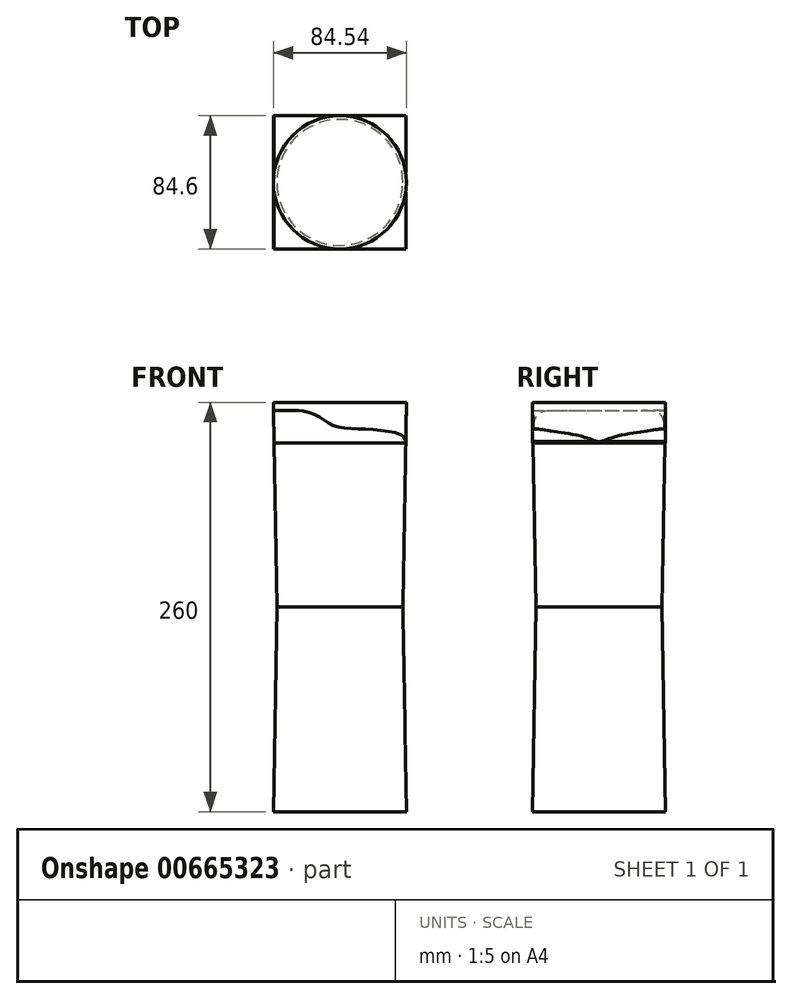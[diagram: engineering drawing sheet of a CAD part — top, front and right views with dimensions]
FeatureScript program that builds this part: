
annotation { "Feature Type Name" : "Feature", "Feature Type Description" : "" }
export const myFeature = defineFeature(function(context is Context, id is Id, definition is map)
    precondition{}
    {
        {
            var Q0;
            Q0=qCreatedBy(makeId("Top.planeOp"),FACE);
            var sketch = newSketch(context, id + "F0", { "sketchPlane" : qUnion([Q0])});
            skCircle(sketch, "E0", {"center": v(0, 0) * mm, "radius": 40 * mm});
            skSolve(sketch);
        }
        {
            var Q0;
            Q0=makeQuery(id+"F0.imprint","IMPRINT",FACE,{"disambiguationData":[TD([[makeQuery(id+"F0.imprint","IMPRINT",EDGE,{"derivedFrom":sQuery(id+"F0.wireOp",EDGE,"E0")}),1.0]])]});
            extrude(context, id + "F1", {"entities" : qUnion([Q0]), "endBound" : BoundingType.SYMMETRIC, "depth" : 260 * mm, "offsetDistance" : 25 * mm, "hasDraft" : true, "draftAngle" : 1 * degree});
        }
        {
            var Q0;
            Q0=qCreatedBy(makeId("Front.planeOp"),FACE);
            var sketch = newSketch(context, id + "F2", { "sketchPlane" : qUnion([Q0])});
            skLineSegment(sketch, "E1", {"start": v(-41.82, 104.3) * mm, "end": v(41.83, 104.3) * mm});
            skLineSegment(sketch, "E2", {"start": v(41.83, 104.3) * mm, "end": v(41.83, 105.18) * mm});
            skFitSpline(sketch, "E3", {"points": [v(41.83, 105.18) * mm, v(39.98, 108.81) * mm, v(17.77, 112.92) * mm, v(-4.2, 115.37) * mm, v(-17.46, 123.04) * mm, v(-41.82, 124.75) * mm], "startDerivative": vector(-6.46, 38.94) * mm, "endDerivative": vector(-110.85, -2.96) * mm});
            skLineSegment(sketch, "E4", {"start": v(-41.82, 124.75) * mm, "end": v(-42.18, 124.73) * mm});
            skLineSegment(sketch, "E5", {"start": v(-42.18, 124.73) * mm, "end": v(-41.82, 104.3) * mm});
            skSolve(sketch);
        }
        {
            var Q0;
            Q0 = qSketchRegion(id + "F2", true);
            extrude(context, id + "F3", {"entities" : qUnion([Q0]), "operationType" : NewBodyOperationType.ADD, "endBound" : BoundingType.SYMMETRIC, "depth" : 84.6 * mm, "offsetDistance" : 25 * mm});
        }
    });
